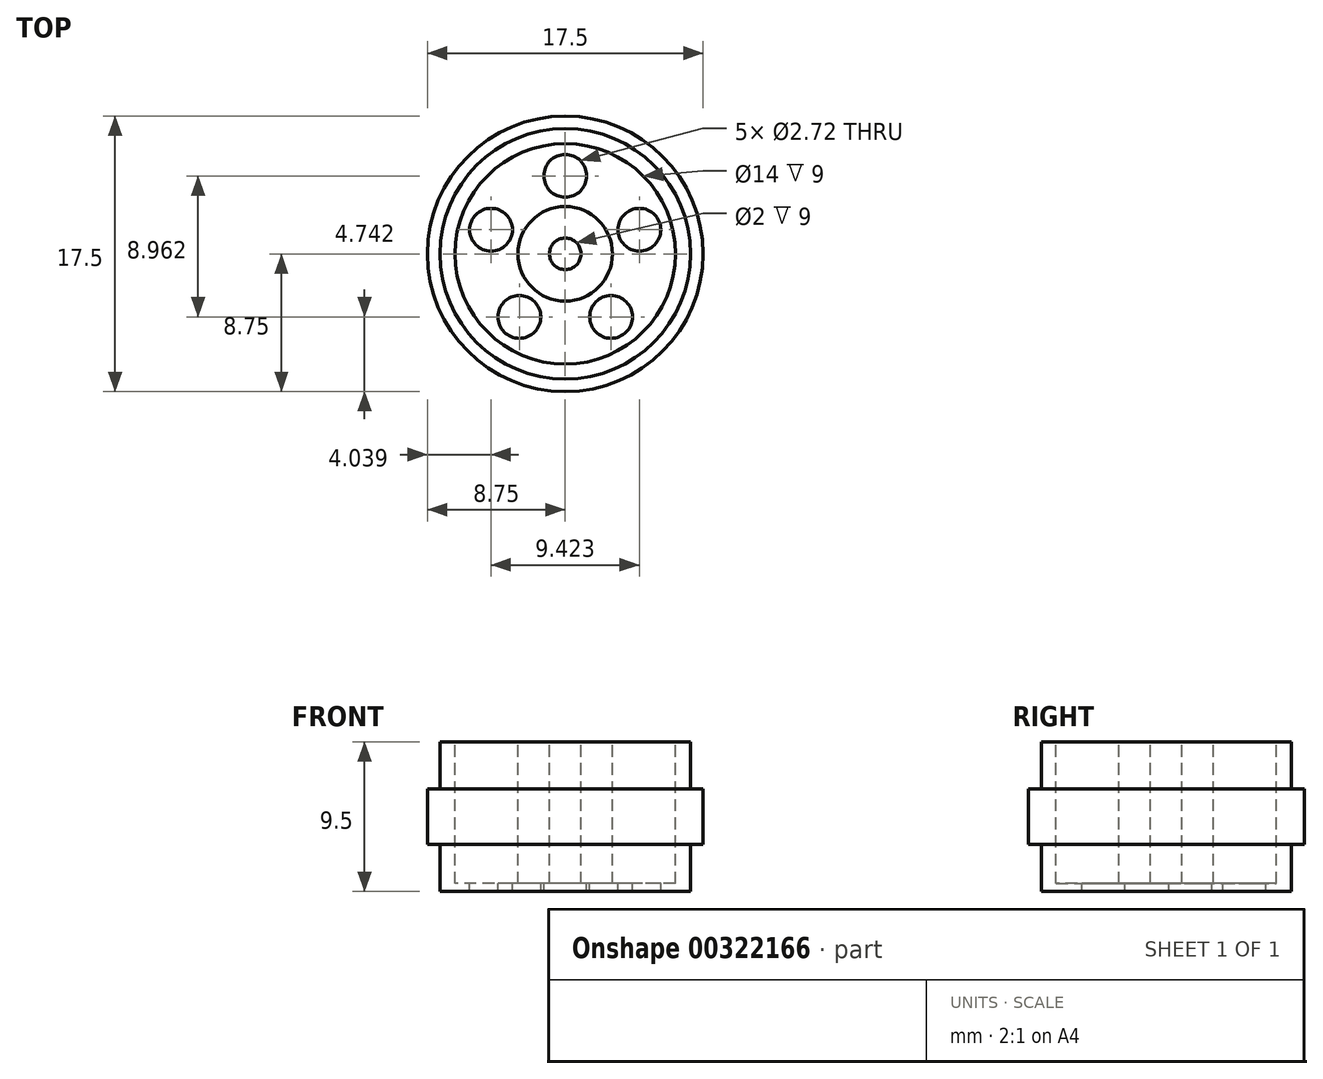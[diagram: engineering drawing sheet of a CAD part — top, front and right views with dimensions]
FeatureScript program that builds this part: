
annotation { "Feature Type Name" : "Feature", "Feature Type Description" : "" }
export const myFeature = defineFeature(function(context is Context, id is Id, definition is map)
    precondition{}
    {
        {
            var Q0;
            Q0=qCreatedBy(makeId("Top.planeOp"),FACE);
            var sketch = newSketch(context, id + "F0", { "sketchPlane" : qUnion([Q0])});
            skCircle(sketch, "E0", {"center": v(0, 0) * mm, "radius": 7.95 * mm});
            skSolve(sketch);
        }
        {
            var Q0;
            Q0 = qSketchRegion(id + "F0", true);
            extrude(context, id + "F1", {"entities" : qUnion([Q0]), "depth" : 3 * mm});
        }
        {
            var Q0;
            Q0=makeQuery(id+"F1.opExtrude","CAP_FACE",FACE,{"disambiguationData":[OSD([sQuery(id+"F0.wireOp",EDGE,"E0")])],"isStart":false});
            var sketch = newSketch(context, id + "F2", { "sketchPlane" : qUnion([Q0])});
            skCircle(sketch, "E1", {"center": v(0, 0) * mm, "radius": 8.75 * mm});
            skSolve(sketch);
        }
        {
            var Q0;
            Q0 = qSketchRegion(id + "F2", true);
            extrude(context, id + "F3", {"entities" : qUnion([Q0]), "operationType" : NewBodyOperationType.ADD, "depth" : 3.5 * mm});
        }
        {
            var Q0;
            Q0=makeQuery(id+"F3.opExtrude","CAP_FACE",FACE,{"disambiguationData":[OSD([sQuery(id+"F2.wireOp",EDGE,"E1")])],"isStart":false});
            var sketch = newSketch(context, id + "F4", { "sketchPlane" : qUnion([Q0])});
            skCircle(sketch, "E2", {"center": v(0, 0) * mm, "radius": 7.95 * mm});
            skSolve(sketch);
        }
        {
            var Q0;
            Q0 = qSketchRegion(id + "F4", true);
            extrude(context, id + "F5", {"entities" : qUnion([Q0]), "operationType" : NewBodyOperationType.ADD, "depth" : 3 * mm});
        }
        {
            var Q0;
            Q0=makeQuery(id+"F5.opExtrude","CAP_FACE",FACE,{"disambiguationData":[OSD([sQuery(id+"F4.wireOp",EDGE,"E2")])],"isStart":false});
            var sketch = newSketch(context, id + "F6", { "sketchPlane" : qUnion([Q0])});
            skCircle(sketch, "E3", {"center": v(0, 4.95) * mm, "radius": 1.36 * mm});
            skCircle(sketch, "E4.1.0", {"center": v(-4.71, 1.53) * mm, "radius": 1.36 * mm});
            skCircle(sketch, "E4.2.0", {"center": v(-2.91, -4) * mm, "radius": 1.36 * mm});
            skCircle(sketch, "E4.3.0", {"center": v(2.91, -4) * mm, "radius": 1.36 * mm});
            skCircle(sketch, "E4.4.0", {"center": v(4.71, 1.53) * mm, "radius": 1.36 * mm});
            skPoint(sketch, "E4.center", {"position": v(0, 0) * mm});
            skSolve(sketch);
        }
        {
            var Q0;
            Q0=qCreatedBy(makeId("Top.planeOp"),FACE);
            var sketch = newSketch(context, id + "F7", { "sketchPlane" : qUnion([Q0])});
            skSolve(sketch);
        }
        {
            var Q0;
            Q0=makeQuery(id+"F6.imprint","IMPRINT",FACE,{"disambiguationData":[TD([[makeQuery(id+"F6.imprint","IMPRINT",EDGE,{"derivedFrom":sQuery(id+"F6.wireOp",EDGE,"E3")}),-1.0]])]});
            var sketch = newSketch(context, id + "F8", { "sketchPlane" : qUnion([Q0])});
            skCircle(sketch, "E5", {"center": v(0, 0) * mm, "radius": 7 * mm});
            skCircle(sketch, "E6", {"center": v(0, 0) * mm, "radius": 3 * mm});
            skCircle(sketch, "E7", {"center": v(0, 0) * mm, "radius": 1 * mm});
            skSolve(sketch);
        }
        {
            var Q0;
            Q0 = qSketchRegion(id + "F6", true);
            var Q1;
            Q1 = qSketchRegion(id + "F7", true);
            extrude(context, id + "F9", {"entities" : qUnion([Q0, Q1]), "operationType" : NewBodyOperationType.REMOVE, "oppositeDirection" : true, "depth" : 20.4 * mm});
        }
        {
            var Q0;
            Q0 = qSketchRegion(id + "F8", true);
            var Q1;
            Q1=makeQuery(id+"F8.imprint","IMPRINT",FACE,{"disambiguationData":[TD([[makeQuery(id+"F8.imprint","IMPRINT",EDGE,{"derivedFrom":sQuery(id+"F8.wireOp",EDGE,"E7")}),1.0]])]});
            extrude(context, id + "F10", {"entities" : qUnion([Q0, Q1]), "operationType" : NewBodyOperationType.REMOVE, "oppositeDirection" : true, "depth" : 9 * mm});
        }
    });
